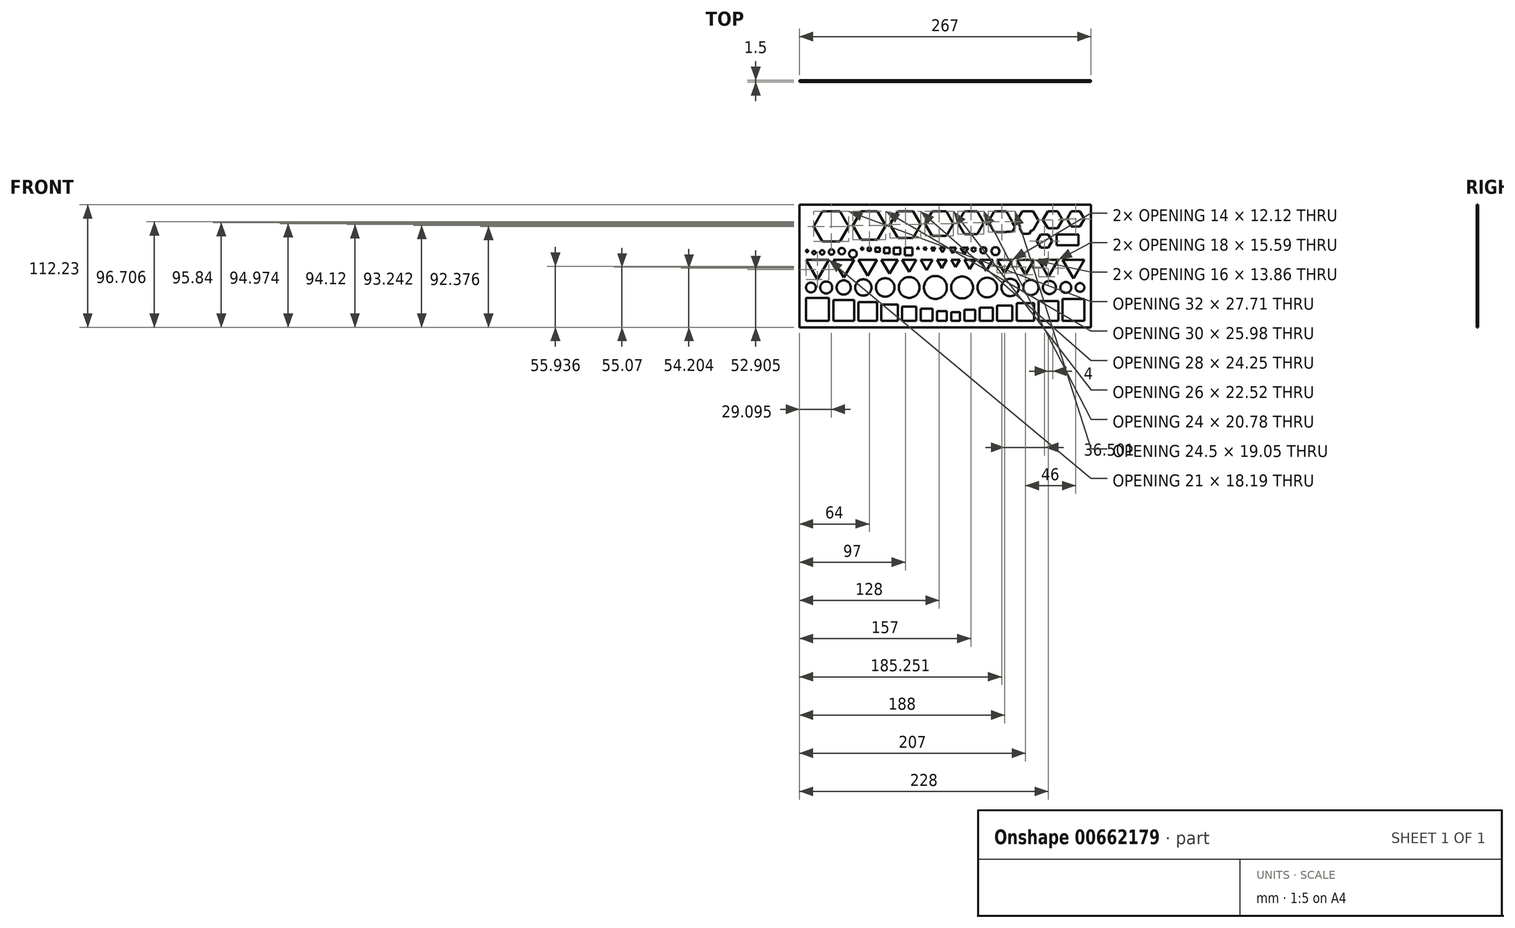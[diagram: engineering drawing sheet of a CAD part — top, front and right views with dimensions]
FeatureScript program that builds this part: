
annotation { "Feature Type Name" : "Feature", "Feature Type Description" : "" }
export const myFeature = defineFeature(function(context is Context, id is Id, definition is map)
    precondition{}
    {
        {
            var Q0;
            Q0=qCreatedBy(makeId("Front.planeOp"),FACE);
            var sketch = newSketch(context, id + "F0", { "sketchPlane" : qUnion([Q0])});
            skLineSegment(sketch, "E0.bottom", {"start": v(0, 0) * mm, "end": v(8, 0) * mm});
            skLineSegment(sketch, "E0.top", {"start": v(0, 8) * mm, "end": v(8, 8) * mm});
            skLineSegment(sketch, "E0.left", {"start": v(0, 0) * mm, "end": v(0, 8) * mm});
            skLineSegment(sketch, "E0.right", {"start": v(8, 0) * mm, "end": v(8, 8) * mm});
            skLineSegment(sketch, "E1.bottom", {"start": v(12, 0) * mm, "end": v(22, 0) * mm});
            skLineSegment(sketch, "E1.top", {"start": v(12, 10) * mm, "end": v(22, 10) * mm});
            skLineSegment(sketch, "E1.left", {"start": v(12, 0) * mm, "end": v(12, 10) * mm});
            skLineSegment(sketch, "E1.right", {"start": v(22, 0) * mm, "end": v(22, 10) * mm});
            skLineSegment(sketch, "E2.bottom", {"start": v(26, 0) * mm, "end": v(38, 0) * mm});
            skLineSegment(sketch, "E2.top", {"start": v(26, 12) * mm, "end": v(38, 12) * mm});
            skLineSegment(sketch, "E2.left", {"start": v(26, 0) * mm, "end": v(26, 12) * mm});
            skLineSegment(sketch, "E2.right", {"start": v(38, 0) * mm, "end": v(38, 12) * mm});
            skLineSegment(sketch, "E3.bottom", {"start": v(42, 0) * mm, "end": v(56, 0) * mm});
            skLineSegment(sketch, "E3.top", {"start": v(42, 14) * mm, "end": v(56, 14) * mm});
            skLineSegment(sketch, "E3.left", {"start": v(42, 0) * mm, "end": v(42, 14) * mm});
            skLineSegment(sketch, "E3.right", {"start": v(56, 0) * mm, "end": v(56, 14) * mm});
            skLineSegment(sketch, "E4.bottom", {"start": v(60, 0) * mm, "end": v(76, 0) * mm});
            skLineSegment(sketch, "E4.top", {"start": v(60, 16) * mm, "end": v(76, 16) * mm});
            skLineSegment(sketch, "E4.left", {"start": v(60, 0) * mm, "end": v(60, 16) * mm});
            skLineSegment(sketch, "E4.right", {"start": v(76, 0) * mm, "end": v(76, 16) * mm});
            skLineSegment(sketch, "E5.bottom", {"start": v(80, 0) * mm, "end": v(98, 0) * mm});
            skLineSegment(sketch, "E5.top", {"start": v(80, 18) * mm, "end": v(98, 18) * mm});
            skLineSegment(sketch, "E5.left", {"start": v(80, 0) * mm, "end": v(80, 18) * mm});
            skLineSegment(sketch, "E5.right", {"start": v(98, 0) * mm, "end": v(98, 18) * mm});
            skLineSegment(sketch, "E6.bottom", {"start": v(102, 0) * mm, "end": v(122, 0) * mm});
            skLineSegment(sketch, "E6.top", {"start": v(102, 20) * mm, "end": v(122, 20) * mm});
            skLineSegment(sketch, "E6.left", {"start": v(102, 0) * mm, "end": v(102, 20) * mm});
            skLineSegment(sketch, "E6.right", {"start": v(122, 0) * mm, "end": v(122, 20) * mm});
            skCircle(sketch, "E7", {"center": v(118, 30.5) * mm, "radius": 4 * mm});
            skCircle(sketch, "E8", {"center": v(105, 30.5) * mm, "radius": 5 * mm});
            skCircle(sketch, "E9", {"center": v(73, 30.5) * mm, "radius": 7 * mm});
            skCircle(sketch, "E10", {"center": v(90, 30.5) * mm, "radius": 6 * mm});
            skCircle(sketch, "E11", {"center": v(54, 30.5) * mm, "radius": 8 * mm});
            skCircle(sketch, "E12", {"center": v(33, 30.5) * mm, "radius": 9 * mm});
            skCircle(sketch, "E13", {"center": v(10, 30.5) * mm, "radius": 10 * mm});
            skLineSegment(sketch, "E14.bottom", {"start": v(-4, 0) * mm, "end": v(-13, 0) * mm});
            skLineSegment(sketch, "E14.top", {"start": v(-4, 9) * mm, "end": v(-13, 9) * mm});
            skLineSegment(sketch, "E14.left", {"start": v(-4, 0) * mm, "end": v(-4, 9) * mm});
            skLineSegment(sketch, "E14.right", {"start": v(-13, 0) * mm, "end": v(-13, 9) * mm});
            skLineSegment(sketch, "E15.bottom", {"start": v(-17, 0) * mm, "end": v(-28, 0) * mm});
            skLineSegment(sketch, "E15.top", {"start": v(-17, 11) * mm, "end": v(-28, 11) * mm});
            skLineSegment(sketch, "E15.left", {"start": v(-17, 0) * mm, "end": v(-17, 11) * mm});
            skLineSegment(sketch, "E15.right", {"start": v(-28, 0) * mm, "end": v(-28, 11) * mm});
            skLineSegment(sketch, "E16.bottom", {"start": v(-32, 0) * mm, "end": v(-45, 0) * mm});
            skLineSegment(sketch, "E16.top", {"start": v(-32, 13) * mm, "end": v(-45, 13) * mm});
            skLineSegment(sketch, "E16.left", {"start": v(-32, 0) * mm, "end": v(-32, 13) * mm});
            skLineSegment(sketch, "E16.right", {"start": v(-45, 0) * mm, "end": v(-45, 13) * mm});
            skLineSegment(sketch, "E17.bottom", {"start": v(-49, 0) * mm, "end": v(-64, 0) * mm});
            skLineSegment(sketch, "E17.top", {"start": v(-49, 15) * mm, "end": v(-64, 15) * mm});
            skLineSegment(sketch, "E17.left", {"start": v(-49, 0) * mm, "end": v(-49, 15) * mm});
            skLineSegment(sketch, "E17.right", {"start": v(-64, 0) * mm, "end": v(-64, 15) * mm});
            skLineSegment(sketch, "E18.bottom", {"start": v(-68, 0) * mm, "end": v(-85, 0) * mm});
            skLineSegment(sketch, "E18.top", {"start": v(-68, 17) * mm, "end": v(-85, 17) * mm});
            skLineSegment(sketch, "E18.left", {"start": v(-68, 0) * mm, "end": v(-68, 17) * mm});
            skLineSegment(sketch, "E18.right", {"start": v(-85, 0) * mm, "end": v(-85, 17) * mm});
            skLineSegment(sketch, "E19.bottom", {"start": v(-89, 0) * mm, "end": v(-108, 0) * mm});
            skLineSegment(sketch, "E19.top", {"start": v(-89, 19) * mm, "end": v(-108, 19) * mm});
            skLineSegment(sketch, "E19.left", {"start": v(-89, 0) * mm, "end": v(-89, 19) * mm});
            skLineSegment(sketch, "E19.right", {"start": v(-108, 0) * mm, "end": v(-108, 19) * mm});
            skLineSegment(sketch, "E20.bottom", {"start": v(-112, 0) * mm, "end": v(-133, 0) * mm});
            skLineSegment(sketch, "E20.top", {"start": v(-112, 21) * mm, "end": v(-133, 21) * mm});
            skLineSegment(sketch, "E20.left", {"start": v(-112, 0) * mm, "end": v(-112, 21) * mm});
            skLineSegment(sketch, "E20.right", {"start": v(-133, 0) * mm, "end": v(-133, 21) * mm});
            skCircle(sketch, "E21", {"center": v(-38.5, 30.5) * mm, "radius": 9.5 * mm});
            skCircle(sketch, "E22", {"center": v(-60.5, 30.5) * mm, "radius": 8.5 * mm});
            skCircle(sketch, "E23", {"center": v(-80.5, 30.5) * mm, "radius": 7.5 * mm});
            skCircle(sketch, "E24", {"center": v(-128.5, 30.5) * mm, "radius": 4.5 * mm});
            skCircle(sketch, "E25", {"center": v(-98.5, 30.5) * mm, "radius": 6.5 * mm});
            skCircle(sketch, "E26", {"center": v(-114.5, 30.5) * mm, "radius": 5.5 * mm});
            skCircle(sketch, "E27", {"center": v(-14.5, 30.5) * mm, "radius": 10.5 * mm});
            skCircle(sketch, "E28.cCircle", {"center": v(4, 53.69) * mm, "radius": 2.3 * mm, "construction": true});
            skLineSegment(sketch, "E28.0", {"start": v(0, 56) * mm, "end": v(8, 56) * mm});
            skLineSegment(sketch, "E28.1", {"start": v(8, 56) * mm, "end": v(4, 49.07) * mm});
            skLineSegment(sketch, "E28.2", {"start": v(4, 49.07) * mm, "end": v(0, 56) * mm});
            skPoint(sketch, "E28.0.midPoint", {"position": v(4, 56) * mm});
            skCircle(sketch, "E29.cCircle", {"center": v(17, 53.11) * mm, "radius": 2.89 * mm, "construction": true});
            skLineSegment(sketch, "E29.0", {"start": v(12, 56) * mm, "end": v(22, 56) * mm});
            skLineSegment(sketch, "E29.1", {"start": v(22, 56) * mm, "end": v(17, 47.34) * mm});
            skLineSegment(sketch, "E29.2", {"start": v(17, 47.34) * mm, "end": v(12, 56) * mm});
            skPoint(sketch, "E29.0.midPoint", {"position": v(17, 56) * mm});
            skCircle(sketch, "E30.cCircle", {"center": v(32, 52.53) * mm, "radius": 3.46 * mm, "construction": true});
            skLineSegment(sketch, "E30.0", {"start": v(26, 56) * mm, "end": v(38, 56) * mm});
            skLineSegment(sketch, "E30.1", {"start": v(38, 56) * mm, "end": v(32, 45.6) * mm});
            skLineSegment(sketch, "E30.2", {"start": v(32, 45.6) * mm, "end": v(26, 56) * mm});
            skPoint(sketch, "E30.0.midPoint", {"position": v(32, 56) * mm});
            skCircle(sketch, "E31.cCircle", {"center": v(49, 51.96) * mm, "radius": 4.04 * mm, "construction": true});
            skLineSegment(sketch, "E31.0", {"start": v(42, 56) * mm, "end": v(56, 56) * mm});
            skLineSegment(sketch, "E31.1", {"start": v(56, 56) * mm, "end": v(49, 43.87) * mm});
            skLineSegment(sketch, "E31.2", {"start": v(49, 43.87) * mm, "end": v(42, 56) * mm});
            skPoint(sketch, "E31.0.midPoint", {"position": v(49, 56) * mm});
            skCircle(sketch, "E32.cCircle", {"center": v(68, 51.38) * mm, "radius": 4.62 * mm, "construction": true});
            skLineSegment(sketch, "E32.0", {"start": v(60, 56) * mm, "end": v(76, 56) * mm});
            skLineSegment(sketch, "E32.1", {"start": v(76, 56) * mm, "end": v(68, 42.14) * mm});
            skLineSegment(sketch, "E32.2", {"start": v(68, 42.14) * mm, "end": v(60, 56) * mm});
            skPoint(sketch, "E32.0.midPoint", {"position": v(68, 56) * mm});
            skCircle(sketch, "E33.cCircle", {"center": v(89, 50.8) * mm, "radius": 5.2 * mm, "construction": true});
            skLineSegment(sketch, "E33.0", {"start": v(80, 56) * mm, "end": v(98, 56) * mm});
            skLineSegment(sketch, "E33.1", {"start": v(98, 56) * mm, "end": v(89, 40.4) * mm});
            skLineSegment(sketch, "E33.2", {"start": v(89, 40.4) * mm, "end": v(80, 56) * mm});
            skPoint(sketch, "E33.0.midPoint", {"position": v(89, 56) * mm});
            skCircle(sketch, "E34.cCircle", {"center": v(112, 50.22) * mm, "radius": 5.77 * mm, "construction": true});
            skLineSegment(sketch, "E34.0", {"start": v(102, 56) * mm, "end": v(122, 56) * mm});
            skLineSegment(sketch, "E34.1", {"start": v(122, 56) * mm, "end": v(112, 38.68) * mm});
            skLineSegment(sketch, "E34.2", {"start": v(112, 38.68) * mm, "end": v(102, 56) * mm});
            skPoint(sketch, "E34.0.midPoint", {"position": v(112, 56) * mm});
            skCircle(sketch, "E35.cCircle", {"center": v(-8.5, 53.4) * mm, "radius": 2.6 * mm, "construction": true});
            skLineSegment(sketch, "E35.0", {"start": v(-13, 56) * mm, "end": v(-4, 56) * mm});
            skLineSegment(sketch, "E35.1", {"start": v(-4, 56) * mm, "end": v(-8.5, 48.2) * mm});
            skLineSegment(sketch, "E35.2", {"start": v(-8.5, 48.2) * mm, "end": v(-13, 56) * mm});
            skPoint(sketch, "E35.0.midPoint", {"position": v(-8.5, 56) * mm});
            skCircle(sketch, "E36.cCircle", {"center": v(-22.5, 52.82) * mm, "radius": 3.18 * mm, "construction": true});
            skLineSegment(sketch, "E36.0", {"start": v(-28, 56) * mm, "end": v(-17, 56) * mm});
            skLineSegment(sketch, "E36.1", {"start": v(-17, 56) * mm, "end": v(-22.5, 46.47) * mm});
            skLineSegment(sketch, "E36.2", {"start": v(-22.5, 46.47) * mm, "end": v(-28, 56) * mm});
            skPoint(sketch, "E36.0.midPoint", {"position": v(-22.5, 56) * mm});
            skCircle(sketch, "E37.cCircle", {"center": v(-38.5, 52.25) * mm, "radius": 3.75 * mm, "construction": true});
            skLineSegment(sketch, "E37.0", {"start": v(-45, 56) * mm, "end": v(-32, 56) * mm});
            skLineSegment(sketch, "E37.1", {"start": v(-32, 56) * mm, "end": v(-38.5, 44.74) * mm});
            skLineSegment(sketch, "E37.2", {"start": v(-38.5, 44.74) * mm, "end": v(-45, 56) * mm});
            skPoint(sketch, "E37.0.midPoint", {"position": v(-38.5, 56) * mm});
            skCircle(sketch, "E38.cCircle", {"center": v(-56.5, 51.67) * mm, "radius": 4.33 * mm, "construction": true});
            skLineSegment(sketch, "E38.0", {"start": v(-64, 56) * mm, "end": v(-49, 56) * mm});
            skLineSegment(sketch, "E38.1", {"start": v(-49, 56) * mm, "end": v(-56.5, 43) * mm});
            skLineSegment(sketch, "E38.2", {"start": v(-56.5, 43) * mm, "end": v(-64, 56) * mm});
            skPoint(sketch, "E38.0.midPoint", {"position": v(-56.5, 56) * mm});
            skCircle(sketch, "E39.cCircle", {"center": v(-76.5, 51.1) * mm, "radius": 4.9 * mm, "construction": true});
            skLineSegment(sketch, "E39.0", {"start": v(-85, 56) * mm, "end": v(-68, 56) * mm});
            skLineSegment(sketch, "E39.1", {"start": v(-68, 56) * mm, "end": v(-76.5, 41.28) * mm});
            skLineSegment(sketch, "E39.2", {"start": v(-76.5, 41.28) * mm, "end": v(-85, 56) * mm});
            skPoint(sketch, "E39.0.midPoint", {"position": v(-76.5, 56) * mm});
            skCircle(sketch, "E40.cCircle", {"center": v(-98.5, 50.51) * mm, "radius": 5.48 * mm, "construction": true});
            skLineSegment(sketch, "E40.0", {"start": v(-108, 56) * mm, "end": v(-89, 56) * mm});
            skLineSegment(sketch, "E40.1", {"start": v(-89, 56) * mm, "end": v(-98.5, 39.54) * mm});
            skLineSegment(sketch, "E40.2", {"start": v(-98.5, 39.54) * mm, "end": v(-108, 56) * mm});
            skPoint(sketch, "E40.0.midPoint", {"position": v(-98.5, 56) * mm});
            skCircle(sketch, "E41.cCircle", {"center": v(-122.5, 49.94) * mm, "radius": 6.06 * mm, "construction": true});
            skLineSegment(sketch, "E41.0", {"start": v(-133, 56) * mm, "end": v(-112, 56) * mm});
            skLineSegment(sketch, "E41.1", {"start": v(-112, 56) * mm, "end": v(-122.5, 37.81) * mm});
            skLineSegment(sketch, "E41.2", {"start": v(-122.5, 37.81) * mm, "end": v(-133, 56) * mm});
            skPoint(sketch, "E41.0.midPoint", {"position": v(-122.5, 56) * mm});
            skCircle(sketch, "E42", {"center": v(-132, 63.92) * mm, "radius": 1 * mm});
            skCircle(sketch, "E43", {"center": v(-125.68, 62.42) * mm, "radius": 1.5 * mm});
            skCircle(sketch, "E44", {"center": v(-118.18, 62.66) * mm, "radius": 2 * mm});
            skCircle(sketch, "E45", {"center": v(-109.69, 62.97) * mm, "radius": 2.5 * mm});
            skCircle(sketch, "E46", {"center": v(-100.22, 63.76) * mm, "radius": 3 * mm});
            skCircle(sketch, "E47", {"center": v(-90, 61.35) * mm, "radius": 3.5 * mm});
            skLineSegment(sketch, "E48.bottom", {"start": v(-82.5, 67) * mm, "end": v(-80.5, 67) * mm});
            skLineSegment(sketch, "E48.top", {"start": v(-82.5, 65) * mm, "end": v(-80.5, 65) * mm});
            skLineSegment(sketch, "E48.left", {"start": v(-82.5, 67) * mm, "end": v(-82.5, 65) * mm});
            skLineSegment(sketch, "E48.right", {"start": v(-80.5, 67) * mm, "end": v(-80.5, 65) * mm});
            skLineSegment(sketch, "E49.bottom", {"start": v(-76.5, 67) * mm, "end": v(-73.5, 67) * mm});
            skLineSegment(sketch, "E49.top", {"start": v(-76.5, 64) * mm, "end": v(-73.5, 64) * mm});
            skLineSegment(sketch, "E49.left", {"start": v(-76.5, 67) * mm, "end": v(-76.5, 64) * mm});
            skLineSegment(sketch, "E49.right", {"start": v(-73.5, 67) * mm, "end": v(-73.5, 64) * mm});
            skLineSegment(sketch, "E50.bottom", {"start": v(-69.5, 67) * mm, "end": v(-65.5, 67) * mm});
            skLineSegment(sketch, "E50.top", {"start": v(-69.5, 63) * mm, "end": v(-65.5, 63) * mm});
            skLineSegment(sketch, "E50.left", {"start": v(-69.5, 67) * mm, "end": v(-69.5, 63) * mm});
            skLineSegment(sketch, "E50.right", {"start": v(-65.5, 67) * mm, "end": v(-65.5, 63) * mm});
            skLineSegment(sketch, "E51.bottom", {"start": v(-61.5, 67) * mm, "end": v(-56.5, 67) * mm});
            skLineSegment(sketch, "E51.top", {"start": v(-61.5, 62) * mm, "end": v(-56.5, 62) * mm});
            skLineSegment(sketch, "E51.left", {"start": v(-61.5, 67) * mm, "end": v(-61.5, 62) * mm});
            skLineSegment(sketch, "E51.right", {"start": v(-56.5, 67) * mm, "end": v(-56.5, 62) * mm});
            skLineSegment(sketch, "E52.bottom", {"start": v(-52.5, 67) * mm, "end": v(-46.5, 67) * mm});
            skLineSegment(sketch, "E52.top", {"start": v(-52.5, 61) * mm, "end": v(-46.5, 61) * mm});
            skLineSegment(sketch, "E52.left", {"start": v(-52.5, 67) * mm, "end": v(-52.5, 61) * mm});
            skLineSegment(sketch, "E52.right", {"start": v(-46.5, 67) * mm, "end": v(-46.5, 61) * mm});
            skLineSegment(sketch, "E53.bottom", {"start": v(-42.5, 67) * mm, "end": v(-35.5, 67) * mm});
            skLineSegment(sketch, "E53.top", {"start": v(-42.5, 60) * mm, "end": v(-35.5, 60) * mm});
            skLineSegment(sketch, "E53.left", {"start": v(-42.5, 67) * mm, "end": v(-42.5, 60) * mm});
            skLineSegment(sketch, "E53.right", {"start": v(-35.5, 67) * mm, "end": v(-35.5, 60) * mm});
            skCircle(sketch, "E54.cCircle", {"center": v(-30.5, 66.42) * mm, "radius": 0.58 * mm, "construction": true});
            skLineSegment(sketch, "E54.0", {"start": v(-31.5, 67) * mm, "end": v(-29.5, 67) * mm});
            skLineSegment(sketch, "E54.1", {"start": v(-29.5, 67) * mm, "end": v(-30.5, 65.26) * mm});
            skLineSegment(sketch, "E54.2", {"start": v(-30.5, 65.26) * mm, "end": v(-31.5, 67) * mm});
            skPoint(sketch, "E54.0.midPoint", {"position": v(-30.5, 67) * mm});
            skCircle(sketch, "E55.cCircle", {"center": v(-24, 66.13) * mm, "radius": 0.87 * mm, "construction": true});
            skLineSegment(sketch, "E55.0", {"start": v(-25.5, 67) * mm, "end": v(-22.5, 67) * mm});
            skLineSegment(sketch, "E55.1", {"start": v(-22.5, 67) * mm, "end": v(-24, 64.4) * mm});
            skLineSegment(sketch, "E55.2", {"start": v(-24, 64.4) * mm, "end": v(-25.5, 67) * mm});
            skPoint(sketch, "E55.0.midPoint", {"position": v(-24, 67) * mm});
            skCircle(sketch, "E56.cCircle", {"center": v(-16.5, 65.84) * mm, "radius": 1.15 * mm, "construction": true});
            skLineSegment(sketch, "E56.0", {"start": v(-18.5, 67) * mm, "end": v(-14.5, 67) * mm});
            skLineSegment(sketch, "E56.1", {"start": v(-14.5, 67) * mm, "end": v(-16.5, 63.53) * mm});
            skLineSegment(sketch, "E56.2", {"start": v(-16.5, 63.53) * mm, "end": v(-18.5, 67) * mm});
            skPoint(sketch, "E56.0.midPoint", {"position": v(-16.5, 67) * mm});
            skCircle(sketch, "E57.cCircle", {"center": v(-8, 65.55) * mm, "radius": 1.44 * mm, "construction": true});
            skLineSegment(sketch, "E57.0", {"start": v(-10.5, 67) * mm, "end": v(-5.5, 67) * mm});
            skLineSegment(sketch, "E57.1", {"start": v(-5.5, 67) * mm, "end": v(-8, 62.67) * mm});
            skLineSegment(sketch, "E57.2", {"start": v(-8, 62.67) * mm, "end": v(-10.5, 67) * mm});
            skPoint(sketch, "E57.0.midPoint", {"position": v(-8, 67) * mm});
            skCircle(sketch, "E58.cCircle", {"center": v(1.5, 65.26) * mm, "radius": 1.73 * mm, "construction": true});
            skLineSegment(sketch, "E58.0", {"start": v(-1.5, 67) * mm, "end": v(4.5, 67) * mm});
            skLineSegment(sketch, "E58.1", {"start": v(4.5, 67) * mm, "end": v(1.5, 61.8) * mm});
            skLineSegment(sketch, "E58.2", {"start": v(1.5, 61.8) * mm, "end": v(-1.5, 67) * mm});
            skPoint(sketch, "E58.0.midPoint", {"position": v(1.5, 67) * mm});
            skCircle(sketch, "E59.cCircle", {"center": v(12, 64.97) * mm, "radius": 2.02 * mm, "construction": true});
            skLineSegment(sketch, "E59.0", {"start": v(8.5, 67) * mm, "end": v(15.5, 67) * mm});
            skLineSegment(sketch, "E59.1", {"start": v(15.5, 67) * mm, "end": v(12, 60.93) * mm});
            skLineSegment(sketch, "E59.2", {"start": v(12, 60.93) * mm, "end": v(8.5, 67) * mm});
            skPoint(sketch, "E59.0.midPoint", {"position": v(12, 67) * mm});
            skCircle(sketch, "E60.cCircle", {"center": v(20.5, 65.26) * mm, "radius": 1.73 * mm, "construction": true});
            skLineSegment(sketch, "E60.0", {"start": v(19.5, 67) * mm, "end": v(21.5, 67) * mm});
            skLineSegment(sketch, "E60.1", {"start": v(21.5, 67) * mm, "end": v(22.5, 65.26) * mm});
            skLineSegment(sketch, "E60.2", {"start": v(22.5, 65.26) * mm, "end": v(21.5, 63.53) * mm});
            skLineSegment(sketch, "E60.3", {"start": v(21.5, 63.53) * mm, "end": v(19.5, 63.53) * mm});
            skLineSegment(sketch, "E60.4", {"start": v(19.5, 63.53) * mm, "end": v(18.5, 65.26) * mm});
            skLineSegment(sketch, "E60.5", {"start": v(18.5, 65.26) * mm, "end": v(19.5, 67) * mm});
            skPoint(sketch, "E60.0.midPoint", {"position": v(20.5, 67) * mm});
            skCircle(sketch, "E61.cCircle", {"center": v(29.5, 64.6) * mm, "radius": 2.6 * mm, "construction": true});
            skLineSegment(sketch, "E61.0", {"start": v(28, 67.2) * mm, "end": v(31, 67.2) * mm});
            skLineSegment(sketch, "E61.1", {"start": v(31, 67.2) * mm, "end": v(32.5, 64.6) * mm});
            skLineSegment(sketch, "E61.2", {"start": v(32.5, 64.6) * mm, "end": v(31, 62) * mm});
            skLineSegment(sketch, "E61.3", {"start": v(31, 62) * mm, "end": v(28, 62) * mm});
            skLineSegment(sketch, "E61.4", {"start": v(28, 62) * mm, "end": v(26.5, 64.6) * mm});
            skLineSegment(sketch, "E61.5", {"start": v(26.5, 64.6) * mm, "end": v(28, 67.2) * mm});
            skPoint(sketch, "E61.0.midPoint", {"position": v(29.5, 67.2) * mm});
            skCircle(sketch, "E62.cCircle", {"center": v(40.5, 63.76) * mm, "radius": 3.46 * mm, "construction": true});
            skLineSegment(sketch, "E62.0", {"start": v(38.5, 67.22) * mm, "end": v(42.5, 67.22) * mm});
            skLineSegment(sketch, "E62.1", {"start": v(42.5, 67.22) * mm, "end": v(44.5, 63.76) * mm});
            skLineSegment(sketch, "E62.2", {"start": v(44.5, 63.76) * mm, "end": v(42.5, 60.3) * mm});
            skLineSegment(sketch, "E62.3", {"start": v(42.5, 60.3) * mm, "end": v(38.5, 60.3) * mm});
            skLineSegment(sketch, "E62.4", {"start": v(38.5, 60.3) * mm, "end": v(36.5, 63.76) * mm});
            skLineSegment(sketch, "E62.5", {"start": v(36.5, 63.76) * mm, "end": v(38.5, 67.22) * mm});
            skPoint(sketch, "E62.0.midPoint", {"position": v(40.5, 67.22) * mm});
            skCircle(sketch, "E63.cCircle", {"center": v(53.5, 85.87) * mm, "radius": 4.33 * mm, "construction": true});
            skLineSegment(sketch, "E63.0", {"start": v(51, 90.2) * mm, "end": v(56, 90.2) * mm});
            skLineSegment(sketch, "E63.1", {"start": v(56, 90.2) * mm, "end": v(58.5, 85.87) * mm});
            skLineSegment(sketch, "E63.2", {"start": v(58.5, 85.87) * mm, "end": v(56, 81.54) * mm});
            skLineSegment(sketch, "E63.3", {"start": v(56, 81.54) * mm, "end": v(51, 81.54) * mm});
            skLineSegment(sketch, "E63.4", {"start": v(51, 81.54) * mm, "end": v(48.5, 85.87) * mm});
            skLineSegment(sketch, "E63.5", {"start": v(48.5, 85.87) * mm, "end": v(51, 90.2) * mm});
            skPoint(sketch, "E63.0.midPoint", {"position": v(53.5, 90.2) * mm});
            skLineSegment(sketch, "E64", {"start": v(-35.5, 67) * mm, "end": v(-78.65, 67) * mm});
            skCircle(sketch, "E65.cCircle", {"center": v(68.5, 85) * mm, "radius": 5.2 * mm, "construction": true});
            skLineSegment(sketch, "E65.0", {"start": v(65.5, 90.2) * mm, "end": v(71.5, 90.2) * mm});
            skLineSegment(sketch, "E65.1", {"start": v(71.5, 90.2) * mm, "end": v(74.5, 85) * mm});
            skLineSegment(sketch, "E65.2", {"start": v(74.5, 85) * mm, "end": v(71.5, 79.8) * mm});
            skLineSegment(sketch, "E65.3", {"start": v(71.5, 79.8) * mm, "end": v(65.5, 79.8) * mm});
            skLineSegment(sketch, "E65.4", {"start": v(65.5, 79.8) * mm, "end": v(62.5, 85) * mm});
            skLineSegment(sketch, "E65.5", {"start": v(62.5, 85) * mm, "end": v(65.5, 90.2) * mm});
            skPoint(sketch, "E65.0.midPoint", {"position": v(68.5, 90.2) * mm});
            skCircle(sketch, "E66.cCircle", {"center": v(85.5, 73.06) * mm, "radius": 6.06 * mm, "construction": true});
            skLineSegment(sketch, "E66.0", {"start": v(82, 79.12) * mm, "end": v(89, 79.12) * mm});
            skLineSegment(sketch, "E66.1", {"start": v(89, 79.12) * mm, "end": v(92.5, 73.06) * mm});
            skLineSegment(sketch, "E66.2", {"start": v(92.5, 73.06) * mm, "end": v(89, 67) * mm});
            skLineSegment(sketch, "E66.3", {"start": v(89, 67) * mm, "end": v(82, 67) * mm});
            skLineSegment(sketch, "E66.4", {"start": v(82, 67) * mm, "end": v(78.5, 73.06) * mm});
            skLineSegment(sketch, "E66.5", {"start": v(78.5, 73.06) * mm, "end": v(82, 79.12) * mm});
            skPoint(sketch, "E66.0.midPoint", {"position": v(85.5, 79.12) * mm});
            skLineSegment(sketch, "E67.bottom", {"start": v(116.5, 79.12) * mm, "end": v(96.5, 79.12) * mm});
            skLineSegment(sketch, "E67.top", {"start": v(116.5, 69.12) * mm, "end": v(96.5, 69.12) * mm});
            skLineSegment(sketch, "E67.left", {"start": v(116.5, 79.12) * mm, "end": v(116.5, 69.12) * mm});
            skLineSegment(sketch, "E67.right", {"start": v(96.5, 79.12) * mm, "end": v(96.5, 69.12) * mm});
            skCircle(sketch, "E68.cCircle", {"center": v(114, 93.3) * mm, "radius": 6.93 * mm, "construction": true});
            skLineSegment(sketch, "E68.0", {"start": v(118, 86.38) * mm, "end": v(110, 86.38) * mm});
            skLineSegment(sketch, "E68.1", {"start": v(110, 86.38) * mm, "end": v(106, 93.3) * mm});
            skLineSegment(sketch, "E68.2", {"start": v(106, 93.3) * mm, "end": v(110, 100.23) * mm});
            skLineSegment(sketch, "E68.3", {"start": v(110, 100.23) * mm, "end": v(118, 100.23) * mm});
            skLineSegment(sketch, "E68.4", {"start": v(118, 100.23) * mm, "end": v(122, 93.3) * mm});
            skLineSegment(sketch, "E68.5", {"start": v(122, 93.3) * mm, "end": v(118, 86.38) * mm});
            skPoint(sketch, "E68.0.midPoint", {"position": v(114, 86.38) * mm});
            skCircle(sketch, "E69.cCircle", {"center": v(93, 92.44) * mm, "radius": 7.8 * mm, "construction": true});
            skLineSegment(sketch, "E69.0", {"start": v(88.5, 100.23) * mm, "end": v(97.5, 100.23) * mm});
            skLineSegment(sketch, "E69.1", {"start": v(97.5, 100.23) * mm, "end": v(102, 92.44) * mm});
            skLineSegment(sketch, "E69.2", {"start": v(102, 92.44) * mm, "end": v(97.5, 84.64) * mm});
            skLineSegment(sketch, "E69.3", {"start": v(97.5, 84.64) * mm, "end": v(88.5, 84.64) * mm});
            skLineSegment(sketch, "E69.4", {"start": v(88.5, 84.64) * mm, "end": v(84, 92.44) * mm});
            skLineSegment(sketch, "E69.5", {"start": v(84, 92.44) * mm, "end": v(88.5, 100.23) * mm});
            skPoint(sketch, "E69.0.midPoint", {"position": v(93, 100.23) * mm});
            skCircle(sketch, "E70.cCircle", {"center": v(70, 91.57) * mm, "radius": 8.66 * mm, "construction": true});
            skLineSegment(sketch, "E70.0", {"start": v(65, 100.23) * mm, "end": v(75, 100.23) * mm});
            skLineSegment(sketch, "E70.1", {"start": v(75, 100.23) * mm, "end": v(80, 91.57) * mm});
            skLineSegment(sketch, "E70.2", {"start": v(80, 91.57) * mm, "end": v(75, 82.91) * mm});
            skLineSegment(sketch, "E70.3", {"start": v(75, 82.91) * mm, "end": v(65, 82.91) * mm});
            skLineSegment(sketch, "E70.4", {"start": v(65, 82.91) * mm, "end": v(60, 91.57) * mm});
            skLineSegment(sketch, "E70.5", {"start": v(60, 91.57) * mm, "end": v(65, 100.23) * mm});
            skPoint(sketch, "E70.0.midPoint", {"position": v(70, 100.23) * mm});
            skCircle(sketch, "E71.cCircle", {"center": v(45, 90.7) * mm, "radius": 9.53 * mm, "construction": true});
            skLineSegment(sketch, "E71.0", {"start": v(39.5, 100.23) * mm, "end": v(50.5, 100.23) * mm});
            skLineSegment(sketch, "E71.1", {"start": v(50.5, 100.23) * mm, "end": v(56, 90.7) * mm});
            skLineSegment(sketch, "E71.2", {"start": v(56, 90.7) * mm, "end": v(50.5, 81.18) * mm});
            skLineSegment(sketch, "E71.3", {"start": v(50.5, 81.18) * mm, "end": v(39.5, 81.18) * mm});
            skLineSegment(sketch, "E71.4", {"start": v(39.5, 81.18) * mm, "end": v(34, 90.7) * mm});
            skLineSegment(sketch, "E71.5", {"start": v(34, 90.7) * mm, "end": v(39.5, 100.23) * mm});
            skPoint(sketch, "E71.0.midPoint", {"position": v(45, 100.23) * mm});
            skCircle(sketch, "E72.cCircle", {"center": v(18, 89.84) * mm, "radius": 10.4 * mm, "construction": true});
            skLineSegment(sketch, "E72.0", {"start": v(12, 100.23) * mm, "end": v(24, 100.23) * mm});
            skLineSegment(sketch, "E72.1", {"start": v(24, 100.23) * mm, "end": v(30, 89.84) * mm});
            skLineSegment(sketch, "E72.2", {"start": v(30, 89.84) * mm, "end": v(24, 79.45) * mm});
            skLineSegment(sketch, "E72.3", {"start": v(24, 79.45) * mm, "end": v(12, 79.45) * mm});
            skLineSegment(sketch, "E72.4", {"start": v(12, 79.45) * mm, "end": v(6, 89.84) * mm});
            skLineSegment(sketch, "E72.5", {"start": v(6, 89.84) * mm, "end": v(12, 100.23) * mm});
            skPoint(sketch, "E72.0.midPoint", {"position": v(18, 100.23) * mm});
            skCircle(sketch, "E73.cCircle", {"center": v(-11, 88.97) * mm, "radius": 11.26 * mm, "construction": true});
            skLineSegment(sketch, "E73.0", {"start": v(-17.5, 100.23) * mm, "end": v(-4.5, 100.23) * mm});
            skLineSegment(sketch, "E73.1", {"start": v(-4.5, 100.23) * mm, "end": v(2, 88.97) * mm});
            skLineSegment(sketch, "E73.2", {"start": v(2, 88.97) * mm, "end": v(-4.5, 77.72) * mm});
            skLineSegment(sketch, "E73.3", {"start": v(-4.5, 77.72) * mm, "end": v(-17.5, 77.72) * mm});
            skLineSegment(sketch, "E73.4", {"start": v(-17.5, 77.72) * mm, "end": v(-24, 88.97) * mm});
            skLineSegment(sketch, "E73.5", {"start": v(-24, 88.97) * mm, "end": v(-17.5, 100.23) * mm});
            skPoint(sketch, "E73.0.midPoint", {"position": v(-11, 100.23) * mm});
            skCircle(sketch, "E74.cCircle", {"center": v(-42, 88.12) * mm, "radius": 12.12 * mm, "construction": true});
            skLineSegment(sketch, "E74.0", {"start": v(-49, 100.24) * mm, "end": v(-35, 100.24) * mm});
            skLineSegment(sketch, "E74.1", {"start": v(-35, 100.24) * mm, "end": v(-28, 88.12) * mm});
            skLineSegment(sketch, "E74.2", {"start": v(-28, 88.12) * mm, "end": v(-35, 76) * mm});
            skLineSegment(sketch, "E74.3", {"start": v(-35, 76) * mm, "end": v(-49, 76) * mm});
            skLineSegment(sketch, "E74.4", {"start": v(-49, 76) * mm, "end": v(-56, 88.12) * mm});
            skLineSegment(sketch, "E74.5", {"start": v(-56, 88.12) * mm, "end": v(-49, 100.24) * mm});
            skPoint(sketch, "E74.0.midPoint", {"position": v(-42, 100.24) * mm});
            skCircle(sketch, "E75.cCircle", {"center": v(-75, 87.24) * mm, "radius": 13 * mm, "construction": true});
            skLineSegment(sketch, "E75.0", {"start": v(-82.5, 100.23) * mm, "end": v(-67.5, 100.23) * mm});
            skLineSegment(sketch, "E75.1", {"start": v(-67.5, 100.23) * mm, "end": v(-60, 87.24) * mm});
            skLineSegment(sketch, "E75.2", {"start": v(-60, 87.24) * mm, "end": v(-67.5, 74.25) * mm});
            skLineSegment(sketch, "E75.3", {"start": v(-67.5, 74.25) * mm, "end": v(-82.5, 74.25) * mm});
            skLineSegment(sketch, "E75.4", {"start": v(-82.5, 74.25) * mm, "end": v(-90, 87.24) * mm});
            skLineSegment(sketch, "E75.5", {"start": v(-90, 87.24) * mm, "end": v(-82.5, 100.23) * mm});
            skPoint(sketch, "E75.0.midPoint", {"position": v(-75, 100.23) * mm});
            skCircle(sketch, "E76.cCircle", {"center": v(-109.9, 86.38) * mm, "radius": 13.86 * mm, "construction": true});
            skLineSegment(sketch, "E76.0", {"start": v(-117.9, 100.23) * mm, "end": v(-101.9, 100.23) * mm});
            skLineSegment(sketch, "E76.1", {"start": v(-101.9, 100.23) * mm, "end": v(-93.9, 86.38) * mm});
            skLineSegment(sketch, "E76.2", {"start": v(-93.9, 86.38) * mm, "end": v(-101.9, 72.52) * mm});
            skLineSegment(sketch, "E76.3", {"start": v(-101.9, 72.52) * mm, "end": v(-117.9, 72.52) * mm});
            skLineSegment(sketch, "E76.4", {"start": v(-117.9, 72.52) * mm, "end": v(-125.9, 86.38) * mm});
            skLineSegment(sketch, "E76.5", {"start": v(-125.9, 86.38) * mm, "end": v(-117.9, 100.23) * mm});
            skPoint(sketch, "E76.0.midPoint", {"position": v(-109.9, 100.23) * mm});
            skLineSegment(sketch, "E77.bottom", {"start": v(-139, 106.23) * mm, "end": v(128, 106.23) * mm});
            skLineSegment(sketch, "E77.top", {"start": v(-139, -6) * mm, "end": v(128, -6) * mm});
            skLineSegment(sketch, "E77.left", {"start": v(-139, 106.23) * mm, "end": v(-139, -6) * mm});
            skLineSegment(sketch, "E77.right", {"start": v(128, 106.23) * mm, "end": v(128, -6) * mm});
            skLineSegment(sketch, "E78", {"start": v(21.5, 67) * mm, "end": v(191.8, 67) * mm});
            skLineSegment(sketch, "E79", {"start": v(-132, 63.92) * mm, "end": v(-80.19, 63.92) * mm});
            skSolve(sketch);
        }
        {
            var Q0;
            Q0=qSketchRegion(id+"F0",true);
            extrude(context, id + "F1", {"entities" : qUnion([Q0]), "depth" : 1.5 * mm, "offsetDistance" : 25 * mm});
        }
    });
